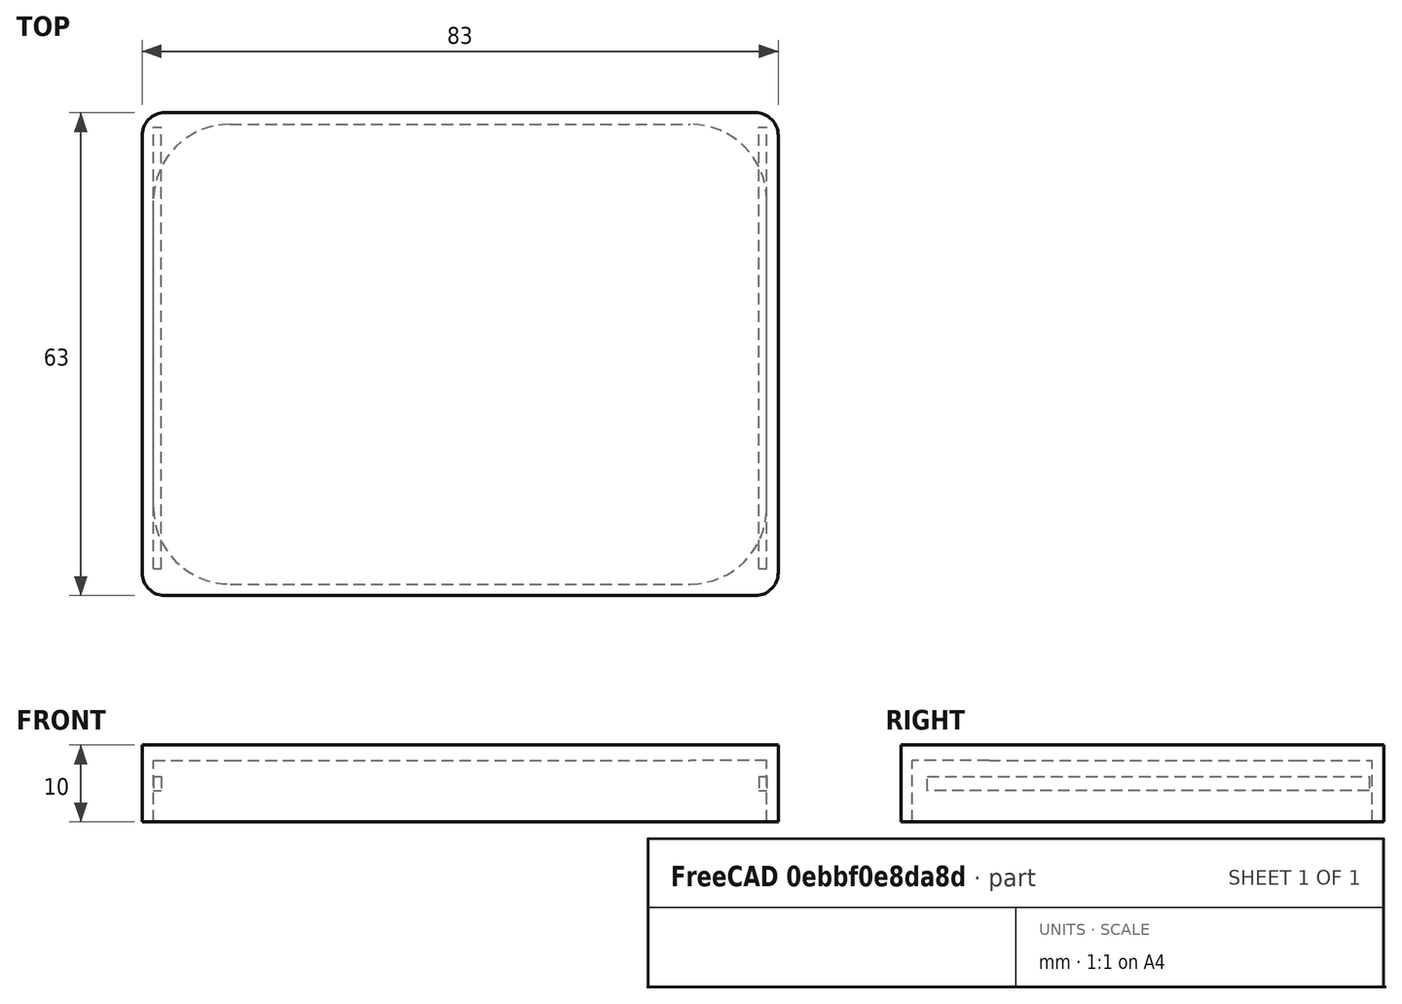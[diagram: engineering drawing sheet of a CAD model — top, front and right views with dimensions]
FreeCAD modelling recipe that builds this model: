
FCSTD DOCUMENT  (FreeCAD 0.19R)
Label: Cover
License: All rights reserved
LicenseURL: http://en.wikipedia.org/wiki/All_rights_reserved
objects: Part::Box×2, Part::Fillet×2, PartDesign::FeatureBase×2, PartDesign::Body×2, Mesh::Feature×2, Spreadsheet::Sheet×1, Mesh::Ellipsoid×1, Part::Cut×1, PartDesign::SubShapeBinder×1, Sketcher::SketchObject×1, PartDesign::Pad×1, Part::Plane×1
note: 14 computed .brp shape members not serialized (recipe doc carries the construction recipe); baked Part::Feature solids carry a one-line shape summary decoded from their .brp

FEATURE [Spreadsheet::Sheet] Spreadsheet  label="SB"
  cells = A1=Height; B1(height)=10; A2=Width; B2(width)=60; A3=Length; B3(length)=80; A4=Border; B4(border)=3
FEATURE [Mesh::Ellipsoid] Ellipsoid
  Placement = pos=(40.5,30.5,-60) rot=(0,0,1;1.5708rad)
  Radius1 = 60
  Radius2 = 80
  Sampling = 50
FEATURE [Part::Box] Box001  label="hole"
  AttacherType = Attacher::AttachEngine3D
  Height = 8
  Length = 80
  Placement = pos=(0.5,0.5,0) rot=(0,0,1;0rad)
  Width = 60
  expr: Width = <<SB>>.width
  expr: Length = <<SB>>.length
FEATURE [Part::Fillet] Fillet
  Base = -> Box001
  Edges = 4 edges r=10: [Edge1,Edge3,Edge5,Edge7]
FEATURE [Part::Box] Box  label="Cube"
  AttacherType = Attacher::AttachEngine3D
  Height = 10
  Length = 83
  Placement = pos=(-1,-1,0) rot=(0,0,1;0rad)
  Width = 63
  expr: Width = <<SB>>.width + 3
  expr: Length = <<SB>>.length + 3
FEATURE [Part::Cut] Cut
  Base = -> Box
  Tool = -> Fillet
FEATURE [Part::Fillet] Fillet001  label="Cover"
  Base = -> Cut
  Edges = 4 edges r=3: [Edge1,Edge3,Edge6,Edge11]
FEATURE [PartDesign::SubShapeBinder] Binder
  BindMode = 0
  ClaimChildren = false
  Context = -> Body [Binder.]
  Fuse = false
  MakeFace = true
  PartialLoad = false
  Relative = true
  Support = -> [Cut[Face14]]
  _Version = 2
FEATURE [PartDesign::FeatureBase] BaseFeature
  BaseFeature = -> Binder
FEATURE [Sketcher::SketchObject] Sketch
  FullyConstrained = false
  MapMode = 5
  Placement = pos=(0.5,0,0) rot=(0.57735,0.57735,0.57735;2.0944rad)
  Support = -> [Cut]
  sketch-geometry (4):
    g0: LineSegment StartX=2.48223 StartY=5.90404 StartZ=0 EndX=60.1041 EndY=5.90404 EndZ=0
    g1: LineSegment StartX=60.1041 StartY=5.90404 StartZ=0 EndX=60.1041 EndY=4.05231 EndZ=0
    g2: LineSegment StartX=60.1041 StartY=4.05231 StartZ=0 EndX=2.48223 EndY=4.05231 EndZ=0
    g3: LineSegment StartX=2.48223 StartY=4.05231 StartZ=0 EndX=2.48223 EndY=5.90404 EndZ=0
  constraints (8):
    c: Coincident(g0,g1)
    c: Coincident(g1,g2)
    c: Coincident(g2,g3)
    c: Coincident(g3,g0)
    c: Horizontal(g0)
    c: Horizontal(g2)
    c: Vertical(g1)
    c: Vertical(g3)
FEATURE [PartDesign::Pad] Pad
  BaseFeature = -> BaseFeature
  Direction = (1,1,1)
  Length = 1
  Length2 = 100
  Profile = -> Sketch
  Type = 0
FEATURE [PartDesign::Body] Body  label="LevSx"
  BaseFeature = -> Binder
  Group = -> [BaseFeature,Binder,Sketch,Pad]
  Origin = -> Origin
  Tip = -> Pad
FEATURE [PartDesign::FeatureBase] Clone
  BaseFeature = -> Pad
  Placement = pos=(79,0,0) rot=(1,0,0;0rad)
FEATURE [PartDesign::Body] Body001  label="LevDx"
  Group = -> [Clone]
  Origin = -> Origin001
  Tip = -> Clone
FEATURE [Mesh::Feature] logo
  Placement = pos=(4,25,22) rot=(0,0,1;0rad)
FEATURE [Mesh::Feature] Difference
FEATURE [Part::Plane] Plane
  AttacherType = Attacher::AttachEngine3D
  Length = 200
  Placement = pos=(-75,-75,9) rot=(0,-0.287348,0.957826;0rad)
  Width = 200
